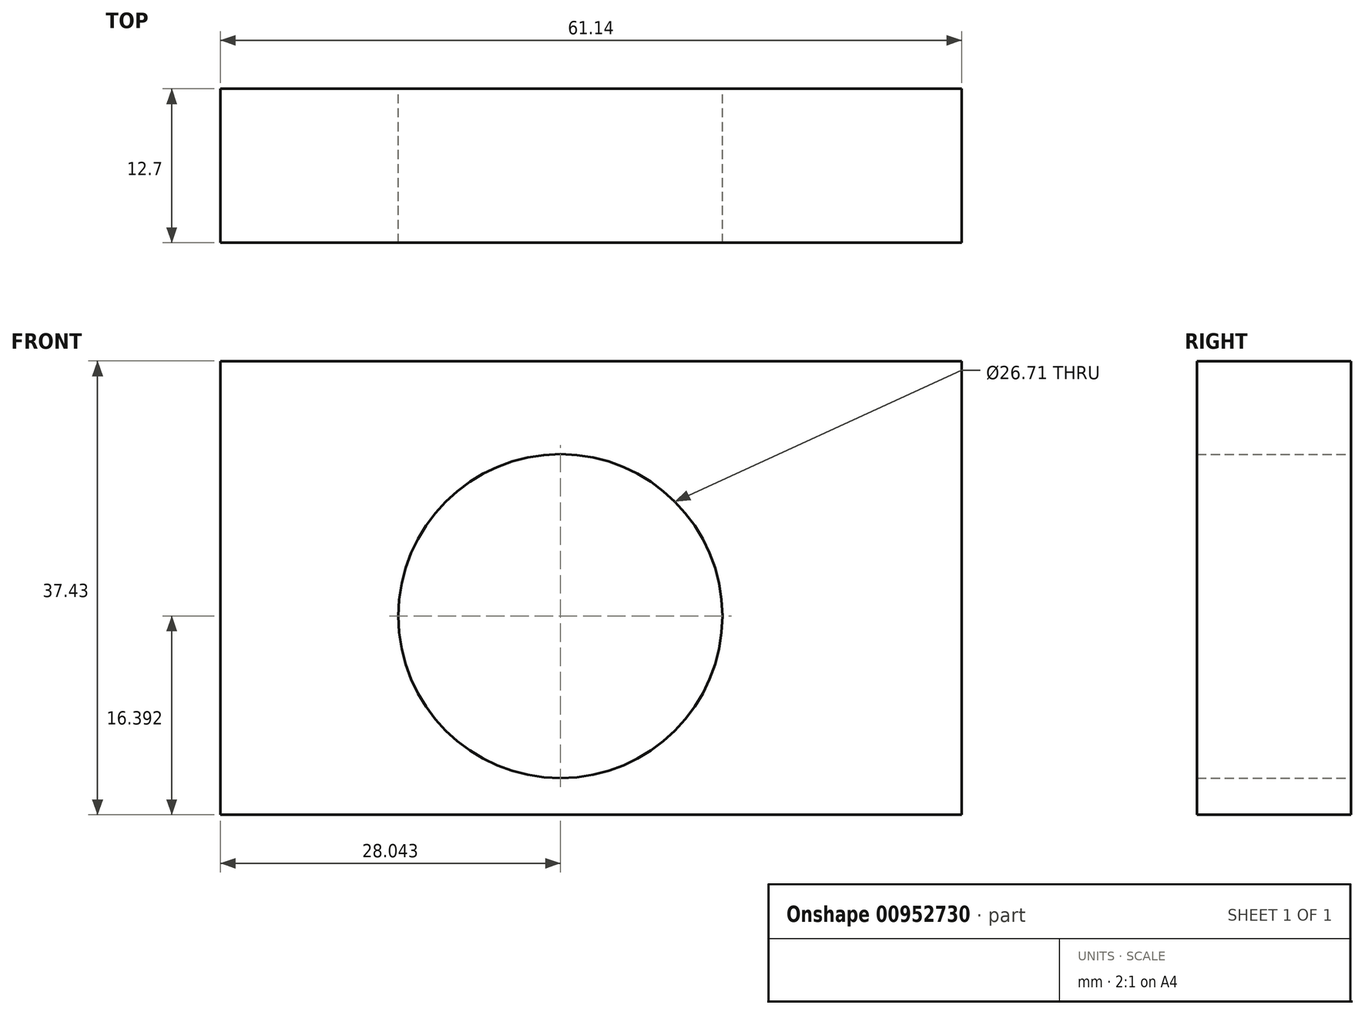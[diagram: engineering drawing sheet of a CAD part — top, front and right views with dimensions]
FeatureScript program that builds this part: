
annotation { "Feature Type Name" : "Feature", "Feature Type Description" : "" }
export const myFeature = defineFeature(function(context is Context, id is Id, definition is map)
    precondition{}
    {
        {
            var Q0;
            Q0=qCreatedBy(makeId("Front.planeOp"),FACE);
            var sketch = newSketch(context, id + "F0", { "sketchPlane" : qUnion([Q0])});
            skLineSegment(sketch, "E0.bottom", {"start": v(0, 0) * mm, "end": v(-61.14, 0) * mm});
            skLineSegment(sketch, "E0.top", {"start": v(0, 37.43) * mm, "end": v(-61.14, 37.43) * mm});
            skLineSegment(sketch, "E0.left", {"start": v(0, 0) * mm, "end": v(0, 37.43) * mm});
            skLineSegment(sketch, "E0.right", {"start": v(-61.14, 0) * mm, "end": v(-61.14, 37.43) * mm});
            skCircle(sketch, "E1", {"center": v(-33.1, 16.4) * mm, "radius": 13.35 * mm});
            skSolve(sketch);
        }
        {
            var Q0;
            Q0 = qSketchRegion(id + "F0", true);
            extrude(context, id + "F1", {"entities" : qUnion([Q0]), "depth" : 12.7 * mm, "offsetDistance" : 25.4 * mm});
        }
    });
